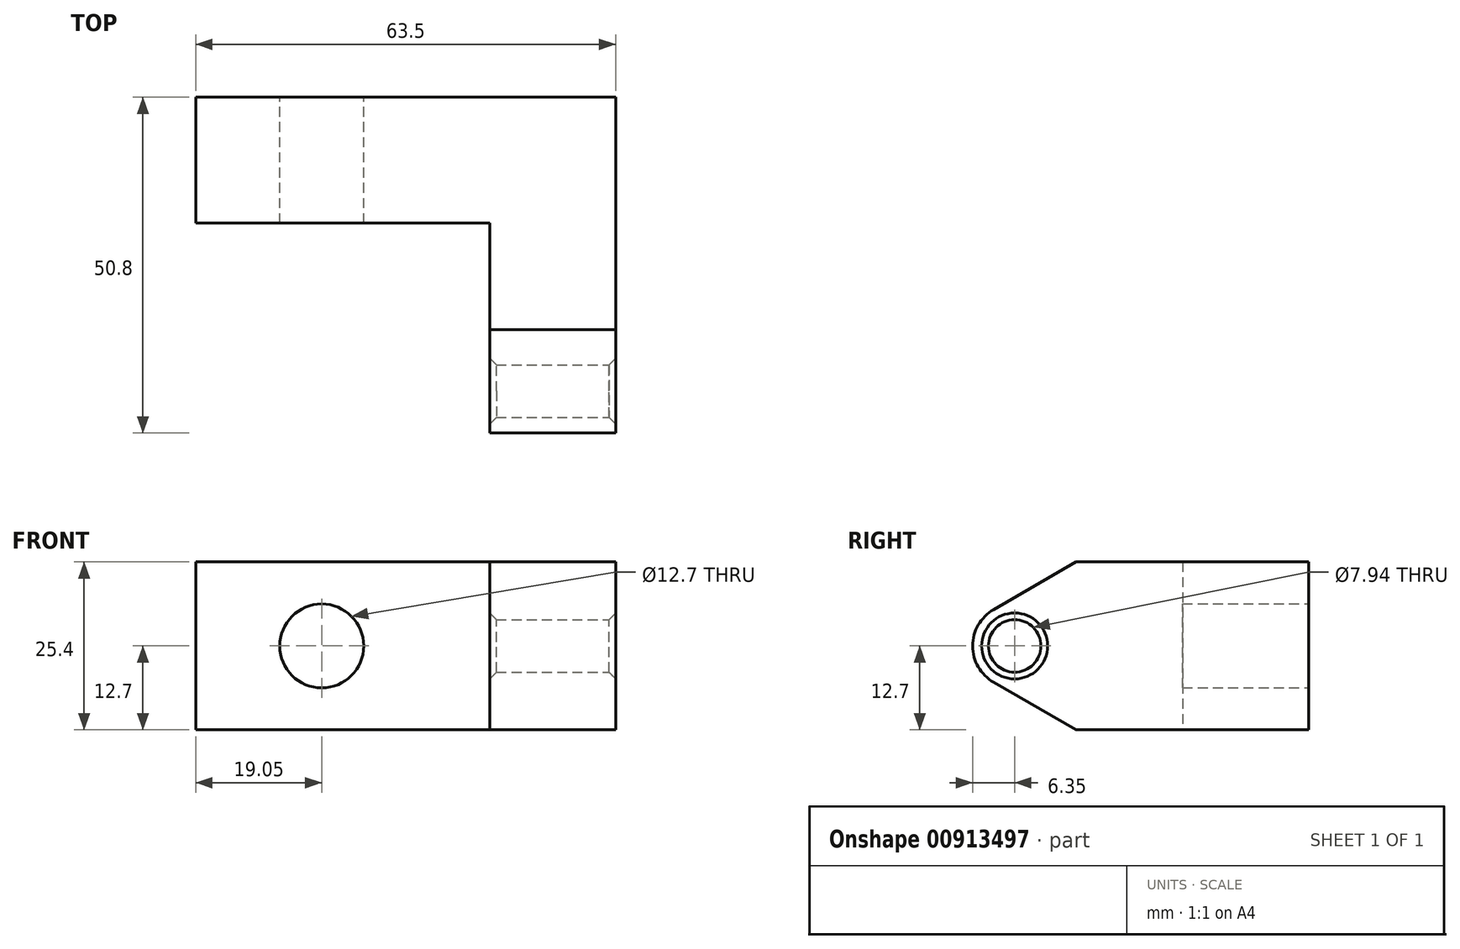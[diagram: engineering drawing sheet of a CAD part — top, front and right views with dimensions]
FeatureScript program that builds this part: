
annotation { "Feature Type Name" : "Feature", "Feature Type Description" : "" }
export const myFeature = defineFeature(function(context is Context, id is Id, definition is map)
    precondition{}
    {
        {
            var Q0;
            Q0=qCreatedBy(makeId("Top.planeOp"),FACE);
            var sketch = newSketch(context, id + "F0", { "sketchPlane" : qUnion([Q0])});
            skLineSegment(sketch, "E0", {"start": v(0, 0) * mm, "end": v(-44.45, 0) * mm});
            skLineSegment(sketch, "E1", {"start": v(-44.45, 0) * mm, "end": v(-44.45, 19.05) * mm});
            skLineSegment(sketch, "E2", {"start": v(-44.45, 19.05) * mm, "end": v(19.05, 19.05) * mm});
            skLineSegment(sketch, "E3", {"start": v(19.05, 19.05) * mm, "end": v(19.05, -31.75) * mm});
            skLineSegment(sketch, "E4", {"start": v(19.05, -31.75) * mm, "end": v(0, -31.75) * mm});
            skLineSegment(sketch, "E5", {"start": v(0, -31.75) * mm, "end": v(0, 0) * mm});
            skSolve(sketch);
        }
        {
            var Q0;
            Q0 = qSketchRegion(id + "F0", true);
            extrude(context, id + "F1", {"entities" : qUnion([Q0]), "depth" : 25.4 * mm, "offsetDistance" : 25.4 * mm});
        }
        {
            var Q0;
            Q0=makeQuery(id+"F1.opExtrude","SWEPT_FACE",FACE,{"disambiguationData":[OSD([sQuery(id+"F0.wireOp",EDGE,"E3")])]});
            var sketch = newSketch(context, id + "F2", { "sketchPlane" : qUnion([Q0])});
            skArc(sketch, "E6", {"start": v(-28.58, 18.2) * mm, "mid": v(-31.75, 12.7) * mm, "end": v(-28.58, 7.2) * mm});
            skPoint(sketch, "E6.centerSnap0", {"position": v(-31.75, 12.7) * mm});
            skLineSegment(sketch, "E7", {"start": v(-16.1, 25.4) * mm, "end": v(-28.58, 18.2) * mm});
            skLineSegment(sketch, "E8", {"start": v(-16.1, 0) * mm, "end": v(-28.58, 7.2) * mm});
            skLineSegment(sketch, "E9", {"start": v(-16.1, 0) * mm, "end": v(-16.1, -5.08) * mm});
            skLineSegment(sketch, "E10", {"start": v(-16.1, -5.08) * mm, "end": v(-41.5, -5.08) * mm});
            skLineSegment(sketch, "E11", {"start": v(-41.5, -5.08) * mm, "end": v(-41.5, 30.48) * mm});
            skLineSegment(sketch, "E12", {"start": v(-41.5, 30.48) * mm, "end": v(-16.1, 30.48) * mm});
            skLineSegment(sketch, "E13", {"start": v(-16.1, 30.48) * mm, "end": v(-16.1, 25.4) * mm});
            skCircle(sketch, "E14", {"center": v(-25.4, 12.7) * mm, "radius": 3.97 * mm});
            skSolve(sketch);
        }
        {
            var Q0;
            Q0 = qSketchRegion(id + "F2", true);
            extrude(context, id + "F3", {"entities" : qUnion([Q0]), "operationType" : NewBodyOperationType.REMOVE, "endBound" : BoundingType.THROUGH_ALL, "oppositeDirection" : true, "depth" : 25.4 * mm, "offsetDistance" : 25.4 * mm});
        }
        {
            var Q0;
            Q0=makeQuery(id+"F1.opExtrude","SWEPT_FACE",FACE,{"disambiguationData":[OSD([sQuery(id+"F0.wireOp",EDGE,"E2")])]});
            var sketch = newSketch(context, id + "F4", { "sketchPlane" : qUnion([Q0])});
            skCircle(sketch, "E15", {"center": v(25.4, 12.7) * mm, "radius": 6.35 * mm});
            skPoint(sketch, "E15.centerSnap0", {"position": v(44.45, 12.7) * mm});
            skSolve(sketch);
        }
        {
            var Q0;
            Q0 = qSketchRegion(id + "F4", true);
            extrude(context, id + "F5", {"entities" : qUnion([Q0]), "operationType" : NewBodyOperationType.REMOVE, "endBound" : BoundingType.THROUGH_ALL, "oppositeDirection" : true, "depth" : 25.4 * mm, "offsetDistance" : 25.4 * mm});
        }
        {
            var Q0;
            Q0=makeQuery(id+"F3.boolean.opBoolean","COPY",FACE,{"derivedFrom":makeQuery(id+"F3.opExtrude","SWEPT_FACE",FACE,{"disambiguationData":[OSD([sQuery(id+"F2.wireOp",EDGE,"E14")])]})});
            chamfer(context, id + "F6", {"entities" : qUnion([Q0]), "width" : 1.02 * mm, "tangentPropagation" : true});
        }
    });
